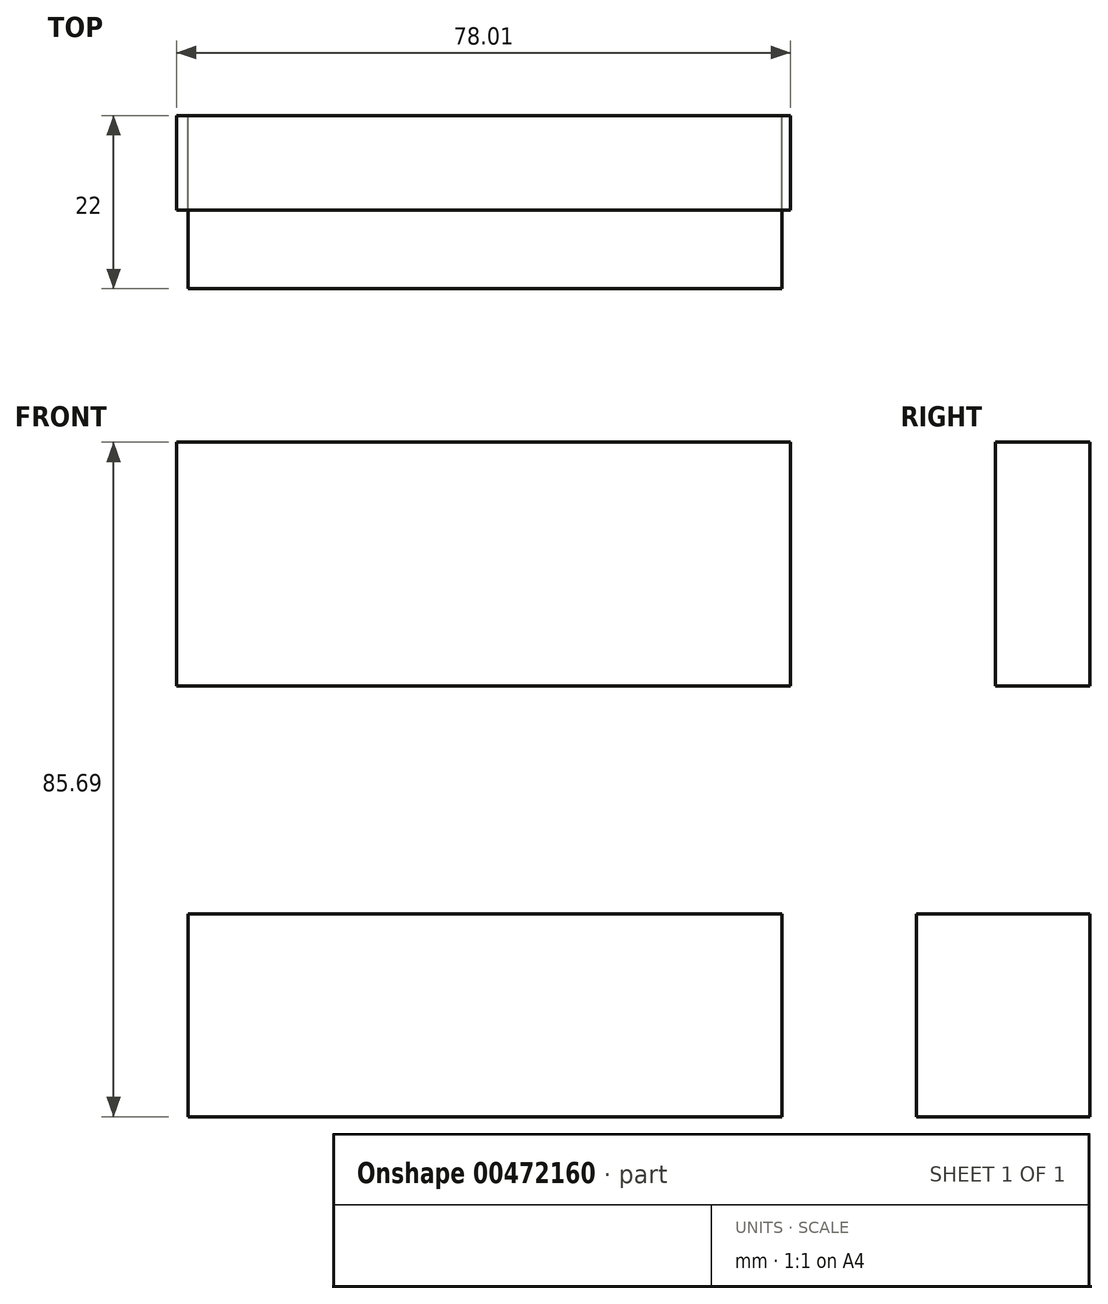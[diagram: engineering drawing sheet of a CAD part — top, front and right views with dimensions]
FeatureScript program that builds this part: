
annotation { "Feature Type Name" : "Feature", "Feature Type Description" : "" }
export const myFeature = defineFeature(function(context is Context, id is Id, definition is map)
    precondition{}
    {
        {
            var Q0;
            Q0=qCreatedBy(makeId("Front.planeOp"),FACE);
            var sketch = newSketch(context, id + "F0", { "sketchPlane" : qUnion([Q0])});
            skSolve(sketch);
        }
        {
            var Q0;
            Q0=qCreatedBy(makeId("Front.planeOp"),FACE);
            var sketch = newSketch(context, id + "F1", { "sketchPlane" : qUnion([Q0])});
            skLineSegment(sketch, "E0.bottom", {"start": v(-90.71, 45.8) * mm, "end": v(-12.7, 45.8) * mm});
            skLineSegment(sketch, "E0.top", {"start": v(-90.71, 14.83) * mm, "end": v(-12.7, 14.83) * mm});
            skLineSegment(sketch, "E0.left", {"start": v(-90.71, 45.8) * mm, "end": v(-90.71, 14.83) * mm});
            skLineSegment(sketch, "E0.right", {"start": v(-12.7, 45.8) * mm, "end": v(-12.7, 14.83) * mm});
            skSolve(sketch);
        }
        {
            var Q0;
            Q0 = qSketchRegion(id + "F0", true);
            var Q1;
            Q1=makeQuery(id+"F1.imprint","IMPRINT",FACE,{"disambiguationData":[TD([[makeQuery(id+"F1.imprint","IMPRINT",EDGE,{"derivedFrom":sQuery(id+"F1.wireOp",EDGE,"E0.bottom")}),-1.0]])]});
            extrude(context, id + "F2", {"entities" : qUnion([Q0, Q1]), "depth" : 12 * mm});
        }
        {
            var Q0;
            Q0=qCreatedBy(makeId("Front.planeOp"),FACE);
            var sketch = newSketch(context, id + "F3", { "sketchPlane" : qUnion([Q0])});
            skLineSegment(sketch, "E1.bottom", {"start": v(-89.22, -14.1) * mm, "end": v(-13.8, -14.1) * mm});
            skLineSegment(sketch, "E1.top", {"start": v(-89.22, -39.88) * mm, "end": v(-13.8, -39.88) * mm});
            skLineSegment(sketch, "E1.left", {"start": v(-89.22, -14.1) * mm, "end": v(-89.22, -39.88) * mm});
            skLineSegment(sketch, "E1.right", {"start": v(-13.8, -14.1) * mm, "end": v(-13.8, -39.88) * mm});
            skSolve(sketch);
        }
        {
            var Q0;
            Q0=makeQuery(id+"F3.imprint","IMPRINT",FACE,{"disambiguationData":[TD([[makeQuery(id+"F3.imprint","IMPRINT",EDGE,{"derivedFrom":sQuery(id+"F3.wireOp",EDGE,"E1.bottom")}),-1.0]])]});
            extrude(context, id + "F4", {"entities" : qUnion([Q0]), "depth" : 22 * mm});
        }
    });
